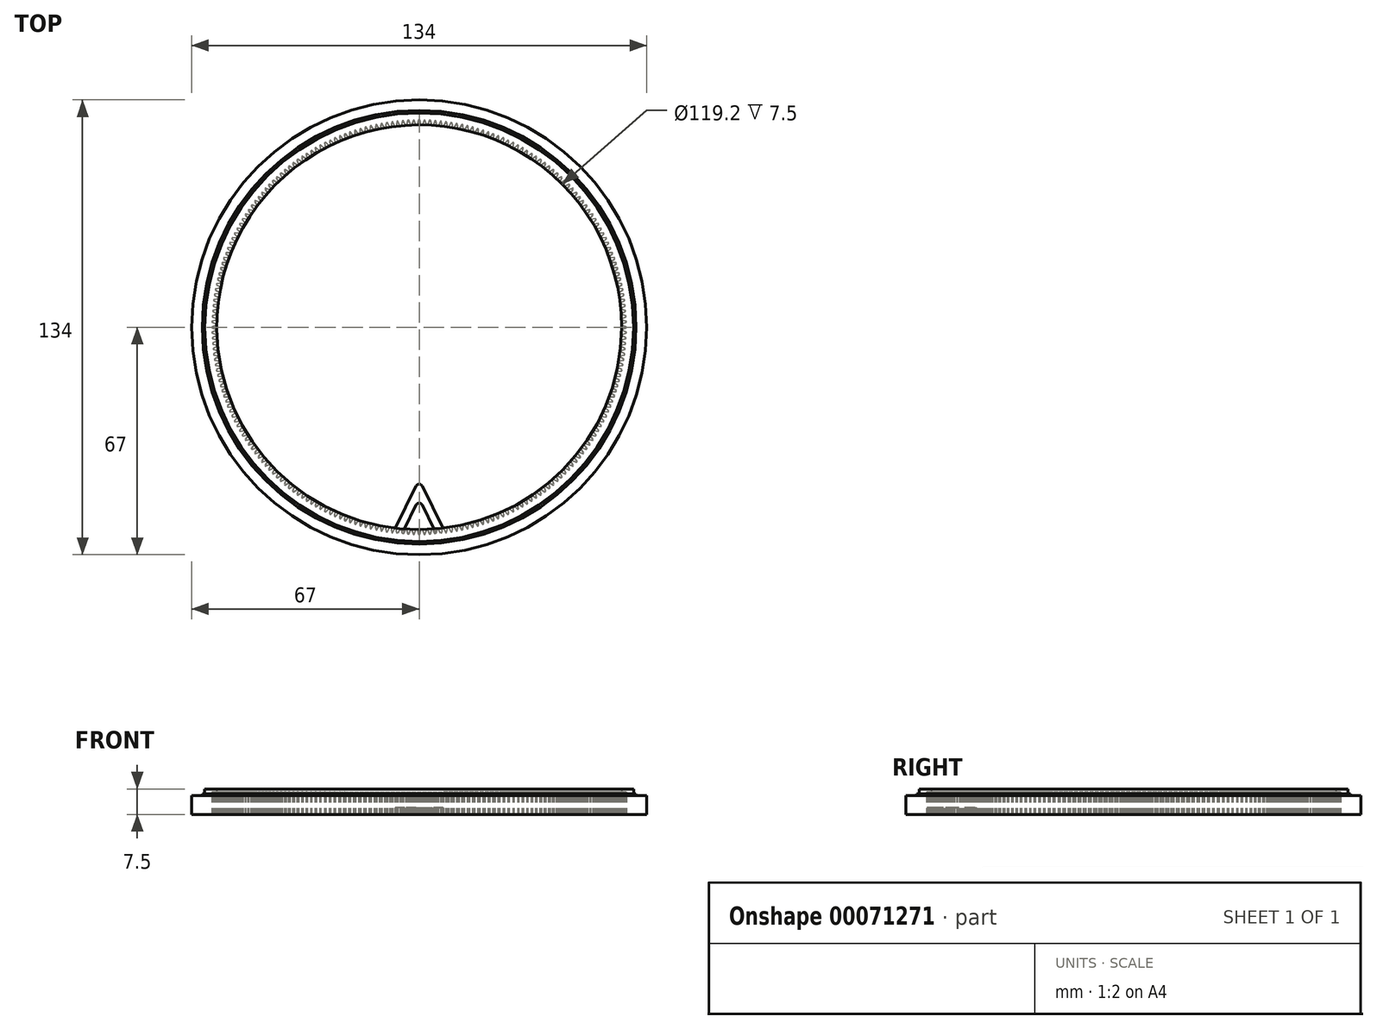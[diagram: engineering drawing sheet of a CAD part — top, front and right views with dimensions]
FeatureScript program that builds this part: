
annotation { "Feature Type Name" : "Feature", "Feature Type Description" : "" }
export const myFeature = defineFeature(function(context is Context, id is Id, definition is map)
    precondition{}
    {
        {
            var Q0;
            Q0=qCreatedBy(makeId("Top.planeOp"),FACE);
            var sketch = newSketch(context, id + "F0", { "sketchPlane" : qUnion([Q0])});
            skCircle(sketch, "E0", {"center": v(0, 0) * mm, "radius": 67 * mm});
            skCircle(sketch, "E1", {"center": v(0, 0) * mm, "radius": 59.6 * mm});
            skSolve(sketch);
        }
        {
            var Q0;
            Q0 = qSketchRegion(id + "F0", true);
            extrude(context, id + "F1", {"entities" : qUnion([Q0]), "endBound" : BoundingType.SYMMETRIC, "depth" : 7.5 * mm});
        }
        {
            var Q0;
            Q0=makeQuery(id+"F1.opExtrude","CAP_FACE",FACE,{"disambiguationData":[OSD([sQuery(id+"F0.wireOp",EDGE,"E0"),sQuery(id+"F0.wireOp",EDGE,"E1")])],"isStart":false});
            var sketch = newSketch(context, id + "F2", { "sketchPlane" : qUnion([Q0])});
            skCircle(sketch, "E2", {"center": v(0, 0) * mm, "radius": 63.88 * mm});
            skCircle(sketch, "E3", {"center": v(0, 0) * mm, "radius": 63.12 * mm});
            skSolve(sketch);
        }
        {
            var Q0;
            Q0=makeQuery(id+"F2.imprint","IMPRINT",FACE,{"disambiguationData":[TD([[makeQuery(id+"F2.imprint","IMPRINT",EDGE,{"derivedFrom":sQuery(id+"F2.wireOp",EDGE,"E2")}),1.0]])]});
            extrude(context, id + "F3", {"entities" : qUnion([Q0]), "operationType" : NewBodyOperationType.REMOVE, "oppositeDirection" : true, "depth" : 1.5 * mm});
        }
        {
            var Q0;
            {var subQ0=sQuery(id+"F0.wireOp",EDGE,"E0");Q0=makeQuery(id+"F3.boolean.opBoolean","SPLIT",FACE,{"disambiguationData":[TD([makeQuery(id+"F1.opExtrude","SWEPT_FACE",FACE,{"disambiguationData":[OSD([subQ0])]})])],"derivedFrom":makeQuery(id+"F1.opExtrude","CAP_FACE",FACE,{"disambiguationData":[OSD([subQ0,sQuery(id+"F0.wireOp",EDGE,"E1")])],"isStart":false})});}
            extrude(context, id + "F4", {"entities" : qUnion([Q0]), "operationType" : NewBodyOperationType.REMOVE, "oppositeDirection" : true, "depth" : 2 * mm});
        }
        {
            var Q0;
            Q0=makeQuery(id+"F1.opExtrude","CAP_FACE",FACE,{"disambiguationData":[OSD([sQuery(id+"F0.wireOp",EDGE,"E0"),sQuery(id+"F0.wireOp",EDGE,"E1")])],"isStart":true});
            var sketch = newSketch(context, id + "F5", { "sketchPlane" : qUnion([Q0])});
            skCircle(sketch, "E4", {"center": v(0, 0) * mm, "radius": 61 * mm, "construction": true});
            skPoint(sketch, "E5", {"position": v(61, 0) * mm});
            skLineSegment(sketch, "E6", {"start": v(0, 0) * mm, "end": v(61, 0) * mm, "construction": true});
            skLineSegment(sketch, "E7", {"start": v(61, 0.15) * mm, "end": v(61, -0.15) * mm});
            skPoint(sketch, "E8", {"position": v(59.4, 0) * mm});
            skLineSegment(sketch, "E9", {"start": v(59.4, 0.67) * mm, "end": v(59.4, -0.67) * mm});
            skLineSegment(sketch, "E10", {"start": v(59.4, 0.68) * mm, "end": v(61, 0.15) * mm});
            skLineSegment(sketch, "E11", {"start": v(61, -0.15) * mm, "end": v(59.4, -0.68) * mm});
            skSolve(sketch);
        }
        {
            var Q0;
            {var subQ0=sQuery(id+"F5.wireOp",EDGE,"E9");Q0=makeQuery(id+"F5.imprint","IMPRINT",FACE,{"disambiguationData":[TD([[makeQuery(id+"F5.imprint","IMPRINT",EDGE,{"derivedFrom":subQ0}),1.0]])]});}
            var Q1;
            {var subQ0=sQuery(id+"F5.wireOp",EDGE,"E7");Q1=makeQuery(id+"F5.imprint","IMPRINT",FACE,{"disambiguationData":[TD([[makeQuery(id+"F5.imprint","IMPRINT",EDGE,{"derivedFrom":subQ0}),-1.0]])]});}
            extrude(context, id + "F6", {"entities" : qUnion([Q0, Q1]), "operationType" : NewBodyOperationType.REMOVE, "oppositeDirection" : true, "depth" : 6.5 * mm});
        }
        {
            var Q0;
            Q0=makeQuery(id+"F6.boolean.opBoolean","COPY",FACE,{"derivedFrom":makeQuery(id+"F6.opExtrude","CAP_FACE",FACE,{"disambiguationData":[OSD([sQuery(id+"F5.wireOp",EDGE,"E7"),sQuery(id+"F5.wireOp",EDGE,"E9"),sQuery(id+"F5.wireOp",EDGE,"E10"),sQuery(id+"F5.wireOp",EDGE,"E11")])],"isStart":false})});
            var Q1;
            Q1=makeQuery(id+"F6.boolean.opBoolean","COPY",FACE,{"derivedFrom":makeQuery(id+"F6.opExtrude","SWEPT_FACE",FACE,{"disambiguationData":[OSD([sQuery(id+"F5.wireOp",EDGE,"E10")])]})});
            var Q2;
            Q2=makeQuery(id+"F6.boolean.opBoolean","COPY",FACE,{"derivedFrom":makeQuery(id+"F6.opExtrude","SWEPT_FACE",FACE,{"disambiguationData":[OSD([sQuery(id+"F5.wireOp",EDGE,"E7")])]})});
            var Q3;
            Q3=makeQuery(id+"F6.boolean.opBoolean","COPY",FACE,{"derivedFrom":makeQuery(id+"F6.opExtrude","SWEPT_FACE",FACE,{"disambiguationData":[OSD([sQuery(id+"F5.wireOp",EDGE,"E11")])]})});
            var Q4;
            Q4=makeQuery(id+"F1.opExtrude","CAP_EDGE",EDGE,{"disambiguationData":[OSD([sQuery(id+"F0.wireOp",EDGE,"E0")])],"isStart":true});
            circularPattern(context, id + "F7", {"faces" : qUnion([Q0, Q1, Q2, Q3]), "axis" : qUnion([Q4]), "angle" : 360 * degree, "instanceCount" : 240, "equalSpace" : true, "patternType" : PatternType.FACE});
        }
        {
            var Q0;
            Q0=makeQuery(id+"F1.opExtrude","CAP_FACE",FACE,{"disambiguationData":[OSD([sQuery(id+"F0.wireOp",EDGE,"E0"),sQuery(id+"F0.wireOp",EDGE,"E1")])],"isStart":true});
            var sketch = newSketch(context, id + "F8", { "sketchPlane" : qUnion([Q0])});
            skCircle(sketch, "E12.0", {"center": v(0, 0) * mm, "radius": 63.12 * mm, "construction": true});
            skLineSegment(sketch, "E13", {"start": v(0, 0) * mm, "end": v(0, 75.26) * mm, "construction": true});
            skLineSegment(sketch, "E14", {"start": v(0, 0) * mm, "end": v(10.99, 78.17) * mm, "construction": true});
            skPoint(sketch, "E15", {"position": v(0, 45) * mm});
            skLineSegment(sketch, "E16", {"start": v(0, 62.52) * mm, "end": v(8.79, 62.52) * mm});
            skLineSegment(sketch, "E17", {"start": v(0, 45) * mm, "end": v(8.79, 62.52) * mm});
            skLineSegment(sketch, "E18.MirrorCS", {"start": v(0, 62.52) * mm, "end": v(-8.79, 62.52) * mm});
            skLineSegment(sketch, "E19.MirrorCS", {"start": v(0, 45) * mm, "end": v(-8.79, 62.52) * mm});
            skLineSegment(sketch, "E20.0", {"start": v(0, 60.02) * mm, "end": v(-4.74, 60.02) * mm});
            skLineSegment(sketch, "E20.1", {"start": v(0, 60.02) * mm, "end": v(4.74, 60.02) * mm});
            skLineSegment(sketch, "E20.2", {"start": v(0, 50.58) * mm, "end": v(4.74, 60.02) * mm});
            skLineSegment(sketch, "E20.3", {"start": v(0, 50.58) * mm, "end": v(-4.74, 60.02) * mm});
            skSolve(sketch);
        }
        {
            var Q0;
            {var subQ0=makeQuery(id+"F7.opPattern","COPY",EDGE,{"derivedFrom":makeQuery(id+"F6.boolean.opBoolean","COPY",EDGE,{"derivedFrom":makeQuery(id+"F6.opExtrude","CAP_EDGE",EDGE,{"disambiguationData":[OSD([sQuery(id+"F5.wireOp",EDGE,"E7")])],"isStart":true})}),"instanceName":"180"});Q0=makeQuery(id+"F8.imprint","IMPRINT",FACE,{"disambiguationData":[TD([[makeQuery(id+"F8.imprint","IMPRINT",EDGE,{"derivedFrom":subQ0}),-1.0]])]});}
            var Q1;
            {var subQ5=makeQuery(id+"F7.opPattern","COPY",EDGE,{"derivedFrom":makeQuery(id+"F6.boolean.opBoolean","COPY",EDGE,{"derivedFrom":makeQuery(id+"F6.opExtrude","CAP_EDGE",EDGE,{"disambiguationData":[OSD([sQuery(id+"F5.wireOp",EDGE,"E7")])],"isStart":true})}),"instanceName":"179"});Q1=makeQuery(id+"F8.imprint","IMPRINT",FACE,{"disambiguationData":[TD([[makeQuery(id+"F8.imprint","IMPRINT",EDGE,{"derivedFrom":subQ5}),-1.0]])]});}
            var Q2;
            {var subQ5=makeQuery(id+"F7.opPattern","COPY",EDGE,{"derivedFrom":makeQuery(id+"F6.boolean.opBoolean","COPY",EDGE,{"derivedFrom":makeQuery(id+"F6.opExtrude","CAP_EDGE",EDGE,{"disambiguationData":[OSD([sQuery(id+"F5.wireOp",EDGE,"E7")])],"isStart":true})}),"instanceName":"178"});Q2=makeQuery(id+"F8.imprint","IMPRINT",FACE,{"disambiguationData":[TD([[makeQuery(id+"F8.imprint","IMPRINT",EDGE,{"derivedFrom":subQ5}),-1.0]])]});}
            var Q3;
            {var subQ5=makeQuery(id+"F7.opPattern","COPY",EDGE,{"derivedFrom":makeQuery(id+"F6.boolean.opBoolean","COPY",EDGE,{"derivedFrom":makeQuery(id+"F6.opExtrude","CAP_EDGE",EDGE,{"disambiguationData":[OSD([sQuery(id+"F5.wireOp",EDGE,"E7")])],"isStart":true})}),"instanceName":"181"});Q3=makeQuery(id+"F8.imprint","IMPRINT",FACE,{"disambiguationData":[TD([[makeQuery(id+"F8.imprint","IMPRINT",EDGE,{"derivedFrom":subQ5}),-1.0]])]});}
            var Q4;
            {var subQ5=makeQuery(id+"F7.opPattern","COPY",EDGE,{"derivedFrom":makeQuery(id+"F6.boolean.opBoolean","COPY",EDGE,{"derivedFrom":makeQuery(id+"F6.opExtrude","CAP_EDGE",EDGE,{"disambiguationData":[OSD([sQuery(id+"F5.wireOp",EDGE,"E7")])],"isStart":true})}),"instanceName":"182"});Q4=makeQuery(id+"F8.imprint","IMPRINT",FACE,{"disambiguationData":[TD([[makeQuery(id+"F8.imprint","IMPRINT",EDGE,{"derivedFrom":subQ5}),-1.0]])]});}
            var Q5;
            {var subQ18=sQuery(id+"F8.wireOp",EDGE,"E16");Q5=makeQuery(id+"F8.imprint","IMPRINT",FACE,{"disambiguationData":[TD([[makeQuery(id+"F8.imprint","IMPRINT",EDGE,{"derivedFrom":subQ18}),-1.0]])]});}
            var Q6;
            {var subQ5=sQuery(id+"F8.wireOp",EDGE,"E20.2");Q6=makeQuery(id+"F8.imprint","IMPRINT",FACE,{"disambiguationData":[TD([[makeQuery(id+"F8.imprint","IMPRINT",EDGE,{"derivedFrom":subQ5}),-1.0]])]});}
            extrude(context, id + "F9", {"entities" : qUnion([Q0, Q1, Q2, Q3, Q4, Q5, Q6]), "operationType" : NewBodyOperationType.ADD, "oppositeDirection" : true, "depth" : 2 * mm});
        }
        {
            var Q0;
            Q0=makeQuery(id+"F9.opExtrude","SWEPT_EDGE",EDGE,{"disambiguationData":[OSD([sQuery(id+"F8.wireOp",EDGE,"E20.2"),sQuery(id+"F8.wireOp",EDGE,"E20.3")])]});
            var Q1;
            Q1=makeQuery(id+"F9.opExtrude","SWEPT_EDGE",EDGE,{"disambiguationData":[OSD([sQuery(id+"F8.wireOp",EDGE,"E17"),sQuery(id+"F8.wireOp",EDGE,"E19.MirrorCS")])]});
            fillet(context, id + "F10", {"entities" : qUnion([Q0, Q1]), "radius" : 1 * mm, "tangentPropagation" : true, "allowEdgeOverflow" : false});
        }
    });
